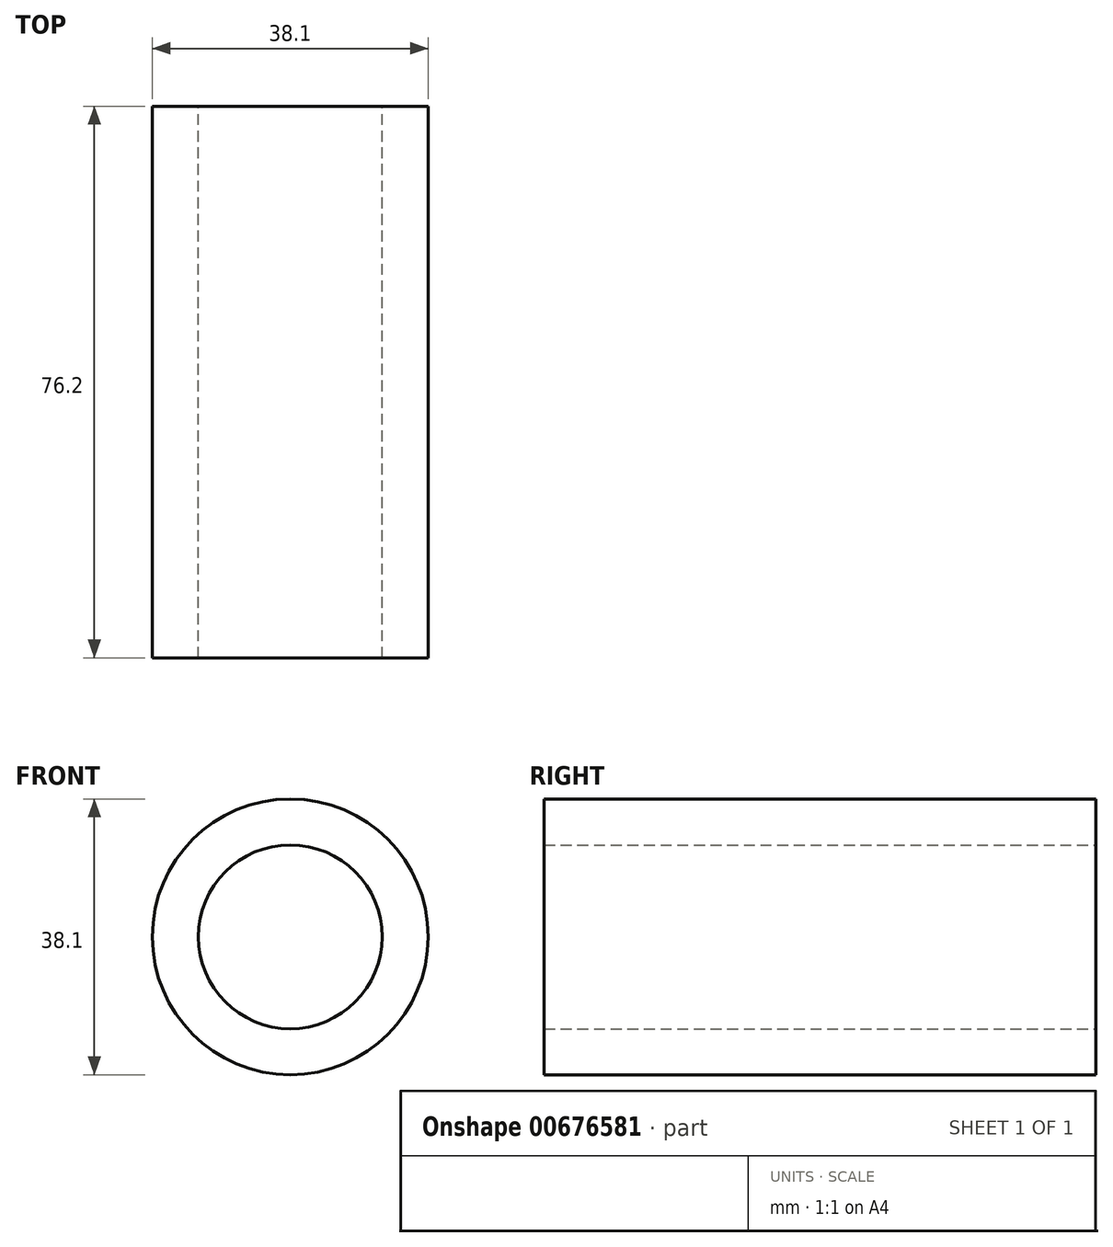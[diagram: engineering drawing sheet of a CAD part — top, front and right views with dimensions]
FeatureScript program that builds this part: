
annotation { "Feature Type Name" : "Feature", "Feature Type Description" : "" }
export const myFeature = defineFeature(function(context is Context, id is Id, definition is map)
    precondition{}
    {
        {
            var Q0;
            Q0=qCreatedBy(makeId("Front.planeOp"),FACE);
            var sketch = newSketch(context, id + "F0", { "sketchPlane" : qUnion([Q0])});
            skCircle(sketch, "E0", {"center": v(0, 0) * mm, "radius": 12.7 * mm});
            skCircle(sketch, "E1", {"center": v(0, 0) * mm, "radius": 19.05 * mm});
            skSolve(sketch);
        }
        {
            var Q0;
            Q0=makeQuery(id+"F0.imprint","IMPRINT",FACE,{"disambiguationData":[TD([[makeQuery(id+"F0.imprint","IMPRINT",EDGE,{"derivedFrom":sQuery(id+"F0.wireOp",EDGE,"E0")}),-1.0]])]});
            extrude(context, id + "F1", {"entities" : qUnion([Q0]), "depth" : 76.2 * mm, "offsetDistance" : 25.4 * mm});
        }
    });
